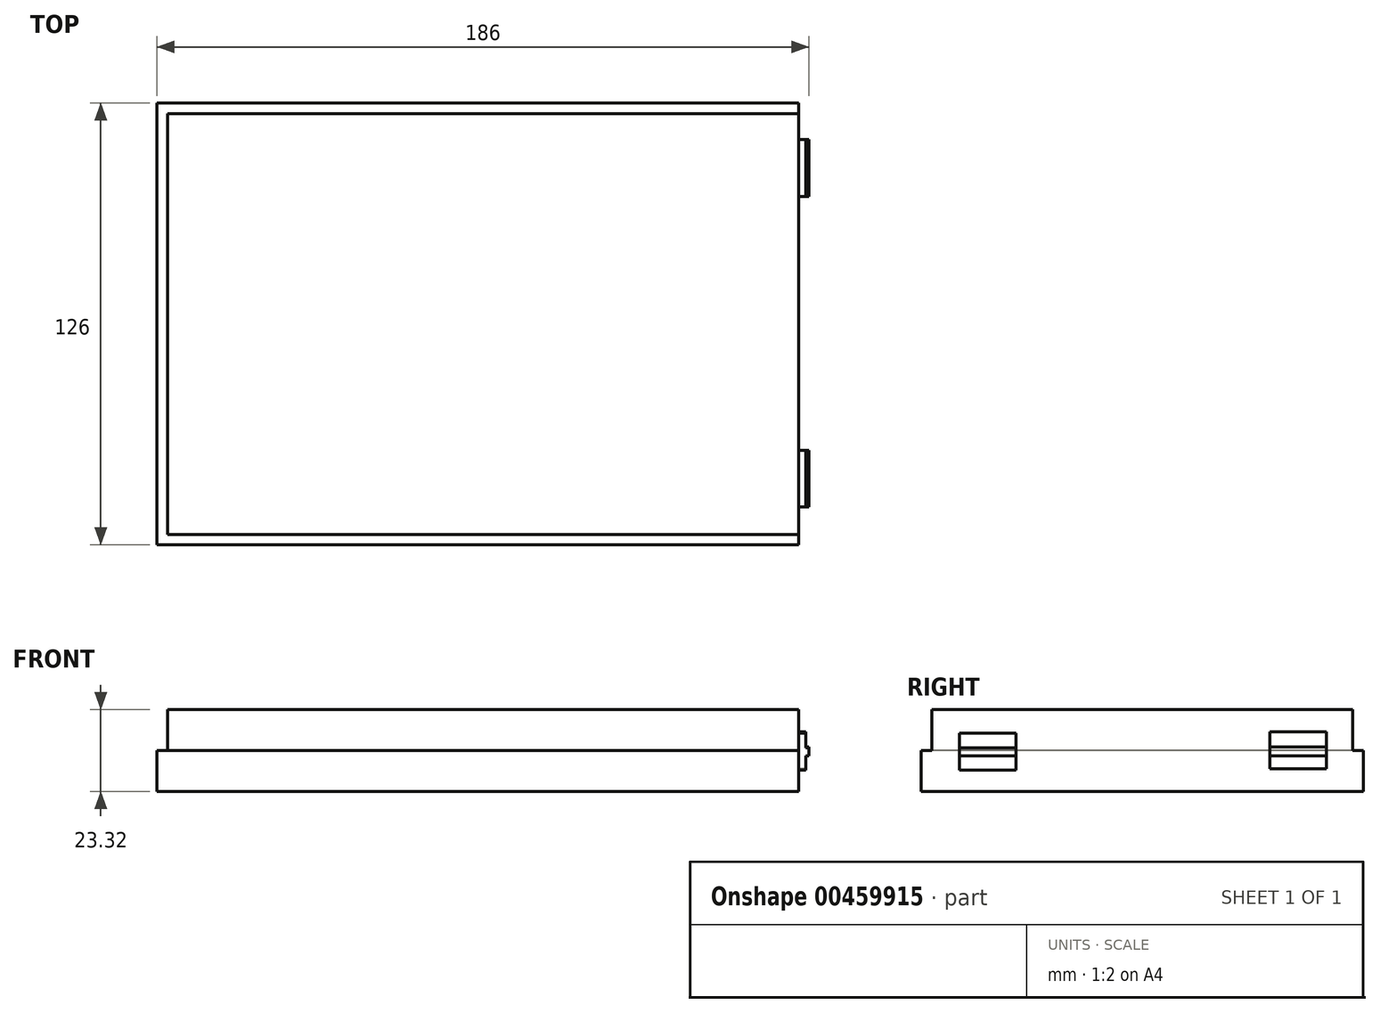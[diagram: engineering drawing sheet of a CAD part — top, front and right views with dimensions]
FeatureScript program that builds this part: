
annotation { "Feature Type Name" : "Feature", "Feature Type Description" : "" }
export const myFeature = defineFeature(function(context is Context, id is Id, definition is map)
    precondition{}
    {
        {
            var Q0;
            Q0=qCreatedBy(makeId("Front.planeOp"),FACE);
            var sketch = newSketch(context, id + "F0", { "sketchPlane" : qUnion([Q0])});
            skLineSegment(sketch, "E0.bottom", {"start": v(-85.66, -2.16) * mm, "end": v(94.34, -2.16) * mm});
            skLineSegment(sketch, "E0.top", {"start": v(-85.66, -25.48) * mm, "end": v(94.34, -25.48) * mm});
            skLineSegment(sketch, "E0.left", {"start": v(-85.66, -2.16) * mm, "end": v(-85.66, -25.48) * mm});
            skLineSegment(sketch, "E0.right", {"start": v(94.34, -2.16) * mm, "end": v(94.34, -25.48) * mm});
            skLineSegment(sketch, "E1", {"start": v(-85.66, -13.82) * mm, "end": v(94.34, -13.82) * mm});
            skSolve(sketch);
        }
        {
            var Q0;
            {var subQ0=sQuery(id+"F0.wireOp",EDGE,"E0.bottom");Q0=makeQuery(id+"F0.imprint","IMPRINT",FACE,{"disambiguationData":[TD([[makeQuery(id+"F0.imprint","IMPRINT",EDGE,{"derivedFrom":subQ0}),-1.0]])]});}
            extrude(context, id + "F1", {"entities" : qUnion([Q0]), "depth" : 120 * mm});
        }
        {
            var Q0;
            {var subQ0=sQuery(id+"F0.wireOp",EDGE,"E0.top");Q0=makeQuery(id+"F0.imprint","IMPRINT",FACE,{"disambiguationData":[TD([[makeQuery(id+"F0.imprint","IMPRINT",EDGE,{"derivedFrom":subQ0}),1.0]])]});}
            extrude(context, id + "F2", {"entities" : qUnion([Q0]), "operationType" : NewBodyOperationType.ADD, "depth" : 123 * mm});
        }
        {
            var Q0;
            {var subQ0=sQuery(id+"F0.wireOp",EDGE,"E0.top");Q0=makeQuery(id+"F0.imprint","IMPRINT",FACE,{"disambiguationData":[TD([[makeQuery(id+"F0.imprint","IMPRINT",EDGE,{"derivedFrom":subQ0}),1.0]])]});}
            extrude(context, id + "F3", {"entities" : qUnion([Q0]), "operationType" : NewBodyOperationType.ADD, "oppositeDirection" : true, "depth" : 3 * mm});
        }
        {
            var Q0;
            {var subQ0=sQuery(id+"F0.wireOp",EDGE,"E0.left");Q0=makeQuery(id+"F3.boolean.opBoolean","MERGE",FACE,{"derivedFrom":[makeQuery(id+"F2.boolean.opBoolean","MERGE",FACE,{"derivedFrom":[makeQuery(id+"F1.opExtrude","SWEPT_FACE",FACE,{"disambiguationData":[OSD([subQ0])]}),makeQuery(id+"F2.opExtrude","SWEPT_FACE",FACE,{"disambiguationData":[OSD([subQ0])]})]}),makeQuery(id+"F3.opExtrude","SWEPT_FACE",FACE,{"disambiguationData":[OSD([subQ0])]})]});}
            var sketch = newSketch(context, id + "F4", { "sketchPlane" : qUnion([Q0])});
            skLineSegment(sketch, "E2", {"start": v(0, -13.82) * mm, "end": v(120, -13.82) * mm});
            skSolve(sketch);
        }
        {
            var Q0;
            Q0=makeQuery(id+"F4.imprint","IMPRINT",FACE,{"disambiguationData":[TD([[makeQuery(id+"F4.imprint","IMPRINT",EDGE,{"derivedFrom":sQuery(id+"F4.wireOp",EDGE,"E2")}),-1.0]])]});
            extrude(context, id + "F5", {"entities" : qUnion([Q0]), "operationType" : NewBodyOperationType.ADD, "depth" : 3 * mm});
        }
        {
            var Q0;
            {var subQ0=sQuery(id+"F0.wireOp",EDGE,"E0.right");Q0=makeQuery(id+"F3.boolean.opBoolean","MERGE",FACE,{"derivedFrom":[makeQuery(id+"F2.boolean.opBoolean","MERGE",FACE,{"derivedFrom":[makeQuery(id+"F1.opExtrude","SWEPT_FACE",FACE,{"disambiguationData":[OSD([subQ0])]}),makeQuery(id+"F2.opExtrude","SWEPT_FACE",FACE,{"disambiguationData":[OSD([subQ0])]})]}),makeQuery(id+"F3.opExtrude","SWEPT_FACE",FACE,{"disambiguationData":[OSD([subQ0])]})]});}
            var sketch = newSketch(context, id + "F6", { "sketchPlane" : qUnion([Q0])});
            skLineSegment(sketch, "E3", {"start": v(-120, -13.82) * mm, "end": v(0, -13.82) * mm, "construction": true});
            skLineSegment(sketch, "E4.bottom", {"start": v(-112.19, -8.84) * mm, "end": v(-96.01, -8.84) * mm});
            skLineSegment(sketch, "E4.top", {"start": v(-112.19, -19.37) * mm, "end": v(-96.01, -19.37) * mm});
            skLineSegment(sketch, "E4.left", {"start": v(-112.19, -8.84) * mm, "end": v(-112.19, -19.37) * mm});
            skLineSegment(sketch, "E4.right", {"start": v(-96.01, -8.84) * mm, "end": v(-96.01, -19.37) * mm});
            skLineSegment(sketch, "E5.bottom", {"start": v(-7.44, -8.46) * mm, "end": v(-23.61, -8.46) * mm});
            skLineSegment(sketch, "E5.top", {"start": v(-7.44, -19) * mm, "end": v(-23.61, -19) * mm});
            skLineSegment(sketch, "E5.left", {"start": v(-7.44, -8.46) * mm, "end": v(-7.44, -19) * mm});
            skLineSegment(sketch, "E5.right", {"start": v(-23.61, -8.46) * mm, "end": v(-23.61, -19) * mm});
            skSolve(sketch);
        }
        {
            var Q0;
            Q0=makeQuery(id+"F6.imprint","IMPRINT",FACE,{"disambiguationData":[TD([[makeQuery(id+"F6.imprint","IMPRINT",EDGE,{"derivedFrom":sQuery(id+"F6.wireOp",EDGE,"E4.bottom")}),-1.0]])]});
            var Q1;
            Q1=makeQuery(id+"F6.imprint","IMPRINT",FACE,{"disambiguationData":[TD([[makeQuery(id+"F6.imprint","IMPRINT",EDGE,{"derivedFrom":sQuery(id+"F6.wireOp",EDGE,"E5.bottom")}),1.0]])]});
            extrude(context, id + "F7", {"entities" : qUnion([Q0, Q1]), "operationType" : NewBodyOperationType.ADD, "depth" : 2 * mm});
        }
        {
            var Q0;
            Q0=makeQuery(id+"F7.opExtrude","CAP_FACE",FACE,{"disambiguationData":[OSD([sQuery(id+"F6.wireOp",EDGE,"E4.bottom"),sQuery(id+"F6.wireOp",EDGE,"E4.top"),sQuery(id+"F6.wireOp",EDGE,"E4.left"),sQuery(id+"F6.wireOp",EDGE,"E4.right")])],"isStart":false});
            var sketch = newSketch(context, id + "F8", { "sketchPlane" : qUnion([Q0])});
            skLineSegment(sketch, "E6.bottom", {"start": v(-112.19, -13.03) * mm, "end": v(-96.01, -13.03) * mm});
            skLineSegment(sketch, "E6.top", {"start": v(-112.19, -15.4) * mm, "end": v(-96.01, -15.4) * mm});
            skLineSegment(sketch, "E6.left", {"start": v(-112.19, -13.03) * mm, "end": v(-112.19, -15.4) * mm});
            skLineSegment(sketch, "E6.right", {"start": v(-96.01, -13.03) * mm, "end": v(-96.01, -15.4) * mm});
            skSolve(sketch);
        }
        {
            var Q0;
            Q0=makeQuery(id+"F8.imprint","IMPRINT",FACE,{"disambiguationData":[TD([[makeQuery(id+"F8.imprint","IMPRINT",EDGE,{"derivedFrom":sQuery(id+"F8.wireOp",EDGE,"E6.bottom")}),-1.0]])]});
            extrude(context, id + "F9", {"entities" : qUnion([Q0]), "operationType" : NewBodyOperationType.ADD, "depth" : 1 * mm});
        }
        {
            var Q0;
            Q0=makeQuery(id+"F7.opExtrude","CAP_FACE",FACE,{"disambiguationData":[OSD([sQuery(id+"F6.wireOp",EDGE,"E5.bottom"),sQuery(id+"F6.wireOp",EDGE,"E5.top"),sQuery(id+"F6.wireOp",EDGE,"E5.left"),sQuery(id+"F6.wireOp",EDGE,"E5.right")])],"isStart":false});
            var sketch = newSketch(context, id + "F10", { "sketchPlane" : qUnion([Q0])});
            skLineSegment(sketch, "E7.bottom", {"start": v(-23.61, -12.83) * mm, "end": v(-7.44, -12.83) * mm});
            skLineSegment(sketch, "E7.top", {"start": v(-23.61, -15.4) * mm, "end": v(-7.44, -15.4) * mm});
            skLineSegment(sketch, "E7.left", {"start": v(-23.61, -12.83) * mm, "end": v(-23.61, -15.4) * mm});
            skLineSegment(sketch, "E7.right", {"start": v(-7.44, -12.83) * mm, "end": v(-7.44, -15.4) * mm});
            skSolve(sketch);
        }
        {
            var Q0;
            Q0=makeQuery(id+"F10.imprint","IMPRINT",FACE,{"disambiguationData":[TD([[makeQuery(id+"F10.imprint","IMPRINT",EDGE,{"derivedFrom":sQuery(id+"F10.wireOp",EDGE,"E7.bottom")}),-1.0]])]});
            extrude(context, id + "F11", {"entities" : qUnion([Q0]), "operationType" : NewBodyOperationType.ADD, "depth" : 1 * mm});
        }
    });
